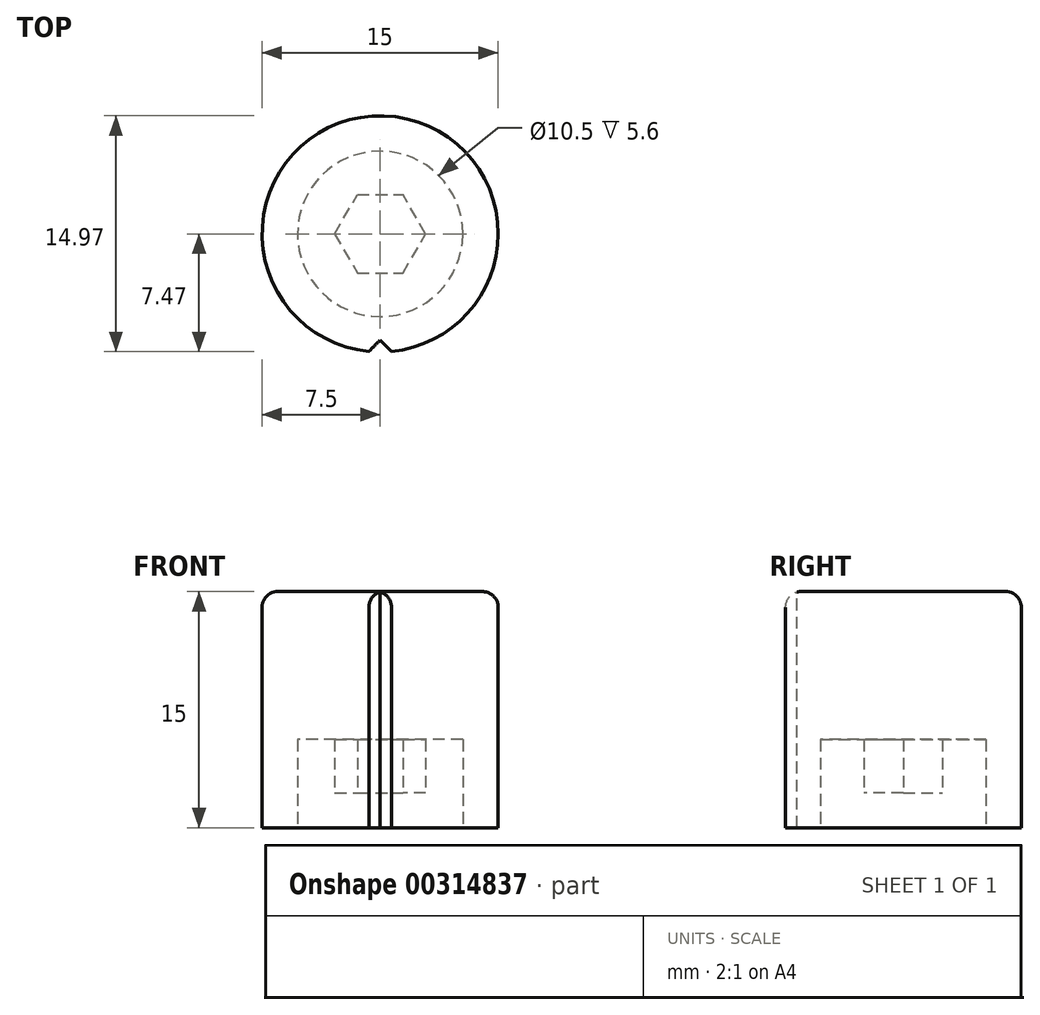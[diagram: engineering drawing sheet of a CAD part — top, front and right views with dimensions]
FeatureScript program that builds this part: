
annotation { "Feature Type Name" : "Feature", "Feature Type Description" : "" }
export const myFeature = defineFeature(function(context is Context, id is Id, definition is map)
    precondition{}
    {
        {
            var Q0;
            Q0=qCreatedBy(makeId("Top.planeOp"),FACE);
            var sketch = newSketch(context, id + "F0", { "sketchPlane" : qUnion([Q0])});
            skCircle(sketch, "E0", {"center": v(0, 0) * mm, "radius": 7.5 * mm});
            skSolve(sketch);
        }
        {
            var Q0;
            Q0 = qSketchRegion(id + "F0", true);
            extrude(context, id + "F1", {"entities" : qUnion([Q0]), "depth" : 15 * mm});
        }
        {
            var Q0;
            Q0=qCreatedBy(makeId("Top.planeOp"),FACE);
            var sketch = newSketch(context, id + "F2", { "sketchPlane" : qUnion([Q0])});
            skCircle(sketch, "E1", {"center": v(0, 0) * mm, "radius": 5.25 * mm});
            skSolve(sketch);
        }
        {
            var Q0;
            Q0 = qSketchRegion(id + "F2", true);
            extrude(context, id + "F3", {"entities" : qUnion([Q0]), "operationType" : NewBodyOperationType.REMOVE, "depth" : 5.6 * mm});
        }
        {
            var Q0;
            Q0=qCreatedBy(makeId("Top.planeOp"),FACE);
            var sketch = newSketch(context, id + "F4", { "sketchPlane" : qUnion([Q0])});
            skCircle(sketch, "E2", {"center": v(0, 0) * mm, "radius": 2.5 * mm, "construction": true});
            skLineSegment(sketch, "E3", {"start": v(-1.44, -2.5) * mm, "end": v(1.44, -2.5) * mm});
            skLineSegment(sketch, "E4", {"start": v(1.44, -2.5) * mm, "end": v(2.89, 0) * mm});
            skLineSegment(sketch, "E5", {"start": v(-1.44, 2.5) * mm, "end": v(1.44, 2.5) * mm});
            skLineSegment(sketch, "E6", {"start": v(2.89, 0) * mm, "end": v(1.44, 2.5) * mm});
            skLineSegment(sketch, "E7", {"start": v(-2.89, 0) * mm, "end": v(-1.44, 2.5) * mm});
            skLineSegment(sketch, "E8", {"start": v(-2.89, 0) * mm, "end": v(-1.44, -2.5) * mm});
            skSolve(sketch);
        }
        {
            var Q0;
            Q0=makeQuery(id+"F1.opExtrude","CAP_EDGE",EDGE,{"disambiguationData":[OSD([sQuery(id+"F0.wireOp",EDGE,"E0")])],"isStart":false});
            fillet(context, id + "F5", {"entities" : qUnion([Q0]), "radius" : 1 * mm, "tangentPropagation" : true, "allowEdgeOverflow" : false});
        }
        {
            var Q0;
            Q0 = qSketchRegion(id + "F4", true);
            extrude(context, id + "F6", {"entities" : qUnion([Q0]), "operationType" : NewBodyOperationType.ADD, "endBound" : BoundingType.UP_TO_NEXT, "depth" : 25 * mm});
        }
        {
            var Q0;
            Q0=makeQuery(id+"F1.opExtrude","CAP_FACE",FACE,{"disambiguationData":[OSD([sQuery(id+"F0.wireOp",EDGE,"E0")])],"isStart":false});
            var sketch = newSketch(context, id + "F7", { "sketchPlane" : qUnion([Q0])});
            skArc(sketch, "E9.0", {"start": v(-0.72, -7.47) * mm, "mid": v(0, -7.5) * mm, "end": v(0.72, -7.47) * mm});
            skLineSegment(sketch, "E10", {"start": v(-0.72, -7.47) * mm, "end": v(0, -6.75) * mm});
            skLineSegment(sketch, "E11", {"start": v(0, -6.75) * mm, "end": v(0.72, -7.47) * mm});
            skSolve(sketch);
        }
        {
            var Q0;
            Q0=qCreatedBy(makeId("Front.planeOp"),FACE);
            var sketch = newSketch(context, id + "F8", { "sketchPlane" : qUnion([Q0])});
            skLineSegment(sketch, "E12", {"start": v(0, 24.51) * mm, "end": v(0, -11.05) * mm});
            skSolve(sketch);
        }
        {
            var Q0;
            Q0 = qSketchRegion(id + "F7", true);
            extrude(context, id + "F9", {"entities" : qUnion([Q0]), "operationType" : NewBodyOperationType.REMOVE, "endBound" : BoundingType.THROUGH_ALL, "oppositeDirection" : true, "depth" : 25 * mm});
        }
        {
            var Q0;
            Q0=makeQuery(id+"F6.opExtrude","CAP_FACE",FACE,{"disambiguationData":[OSD([sQuery(id+"F4.wireOp",EDGE,"E3"),sQuery(id+"F4.wireOp",EDGE,"E4"),sQuery(id+"F4.wireOp",EDGE,"E5"),sQuery(id+"F4.wireOp",EDGE,"E6"),sQuery(id+"F4.wireOp",EDGE,"E7"),sQuery(id+"F4.wireOp",EDGE,"E8")])],"isStart":true});
            extrude(context, id + "F10", {"entities" : qUnion([Q0]), "operationType" : NewBodyOperationType.REMOVE, "oppositeDirection" : true, "depth" : 2.2 * mm});
        }
    });
